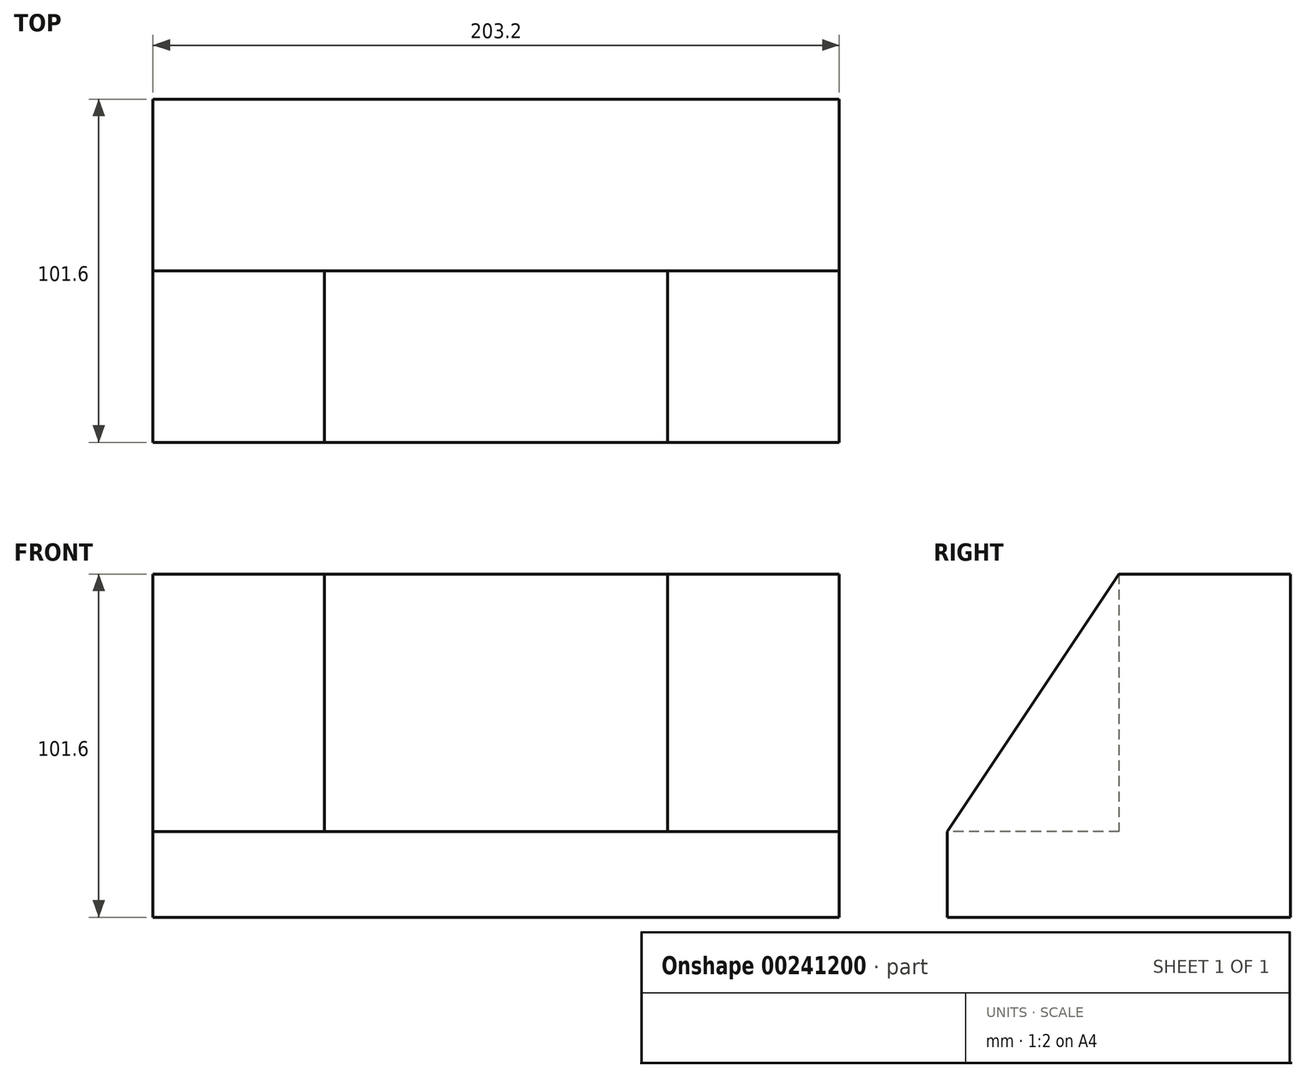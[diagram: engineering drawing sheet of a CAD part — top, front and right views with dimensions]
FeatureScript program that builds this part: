
annotation { "Feature Type Name" : "Feature", "Feature Type Description" : "" }
export const myFeature = defineFeature(function(context is Context, id is Id, definition is map)
    precondition{}
    {
        {
            var Q0;
            Q0=qCreatedBy(makeId("Front.planeOp"),FACE);
            var sketch = newSketch(context, id + "F0", { "sketchPlane" : qUnion([Q0])});
            skLineSegment(sketch, "E0.bottom", {"start": v(-141.1, 72.45) * mm, "end": v(62.1, 72.45) * mm});
            skLineSegment(sketch, "E0.top", {"start": v(-141.1, -29.15) * mm, "end": v(62.1, -29.15) * mm});
            skLineSegment(sketch, "E0.left", {"start": v(-141.1, 72.45) * mm, "end": v(-141.1, -29.15) * mm});
            skLineSegment(sketch, "E0.right", {"start": v(62.1, 72.45) * mm, "end": v(62.1, -29.15) * mm});
            skSolve(sketch);
        }
        {
            var Q0;
            Q0=makeQuery(id+"F0.imprint","IMPRINT",FACE,{"disambiguationData":[TD([[makeQuery(id+"F0.imprint","IMPRINT",EDGE,{"derivedFrom":sQuery(id+"F0.wireOp",EDGE,"E0.bottom")}),-1.0]])]});
            extrude(context, id + "F1", {"entities" : qUnion([Q0]), "depth" : 101.6 * mm});
        }
        {
            var Q0;
            Q0=makeQuery(id+"F1.opExtrude","CAP_FACE",FACE,{"disambiguationData":[OSD([sQuery(id+"F0.wireOp",EDGE,"E0.bottom"),sQuery(id+"F0.wireOp",EDGE,"E0.top"),sQuery(id+"F0.wireOp",EDGE,"E0.left"),sQuery(id+"F0.wireOp",EDGE,"E0.right")])],"isStart":false});
            var sketch = newSketch(context, id + "F2", { "sketchPlane" : qUnion([Q0])});
            skLineSegment(sketch, "E1.bottom", {"start": v(-90.3, 72.45) * mm, "end": v(11.3, 72.45) * mm});
            skLineSegment(sketch, "E1.top", {"start": v(-90.3, -3.75) * mm, "end": v(11.3, -3.75) * mm});
            skLineSegment(sketch, "E1.left", {"start": v(-90.3, 72.45) * mm, "end": v(-90.3, -3.75) * mm});
            skLineSegment(sketch, "E1.right", {"start": v(11.3, 72.45) * mm, "end": v(11.3, -3.75) * mm});
            skSolve(sketch);
        }
        {
            var Q0;
            Q0=makeQuery(id+"F2.imprint","IMPRINT",FACE,{"disambiguationData":[TD([[makeQuery(id+"F2.imprint","IMPRINT",EDGE,{"derivedFrom":sQuery(id+"F2.wireOp",EDGE,"E1.bottom")}),-1.0]])]});
            extrude(context, id + "F3", {"entities" : qUnion([Q0]), "operationType" : NewBodyOperationType.REMOVE, "oppositeDirection" : true, "depth" : 50.8 * mm});
        }
        {
            var Q0;
            Q0=makeQuery(id+"F3.boolean.opBoolean","COPY",FACE,{"derivedFrom":makeQuery(id+"F3.opExtrude","SWEPT_FACE",FACE,{"disambiguationData":[OSD([sQuery(id+"F2.wireOp",EDGE,"E1.left")])]})});
            var sketch = newSketch(context, id + "F4", { "sketchPlane" : qUnion([Q0])});
            skLineSegment(sketch, "E2", {"start": v(-101.6, -3.75) * mm, "end": v(-50.8, 72.45) * mm});
            skSolve(sketch);
        }
        {
            var Q0;
            Q0=makeQuery(id+"F4.imprint","IMPRINT",FACE,{"disambiguationData":[TD([[makeQuery(id+"F4.imprint","IMPRINT",EDGE,{"derivedFrom":sQuery(id+"F4.wireOp",EDGE,"E2")}),1.0]])]});
            extrude(context, id + "F5", {"entities" : qUnion([Q0]), "operationType" : NewBodyOperationType.REMOVE, "oppositeDirection" : true, "depth" : 50.8 * mm});
        }
        {
            var Q0;
            Q0=makeQuery(id+"F3.boolean.opBoolean","COPY",FACE,{"derivedFrom":makeQuery(id+"F3.opExtrude","SWEPT_FACE",FACE,{"disambiguationData":[OSD([sQuery(id+"F2.wireOp",EDGE,"E1.right")])]})});
            var sketch = newSketch(context, id + "F6", { "sketchPlane" : qUnion([Q0])});
            skLineSegment(sketch, "E3", {"start": v(50.8, 72.45) * mm, "end": v(101.6, -3.75) * mm});
            skSolve(sketch);
        }
        {
            var Q0;
            Q0=makeQuery(id+"F6.imprint","IMPRINT",FACE,{"disambiguationData":[TD([[makeQuery(id+"F6.imprint","IMPRINT",EDGE,{"derivedFrom":sQuery(id+"F6.wireOp",EDGE,"E3")}),1.0]])]});
            extrude(context, id + "F7", {"entities" : qUnion([Q0]), "operationType" : NewBodyOperationType.REMOVE, "oppositeDirection" : true, "depth" : 50.8 * mm});
        }
    });
